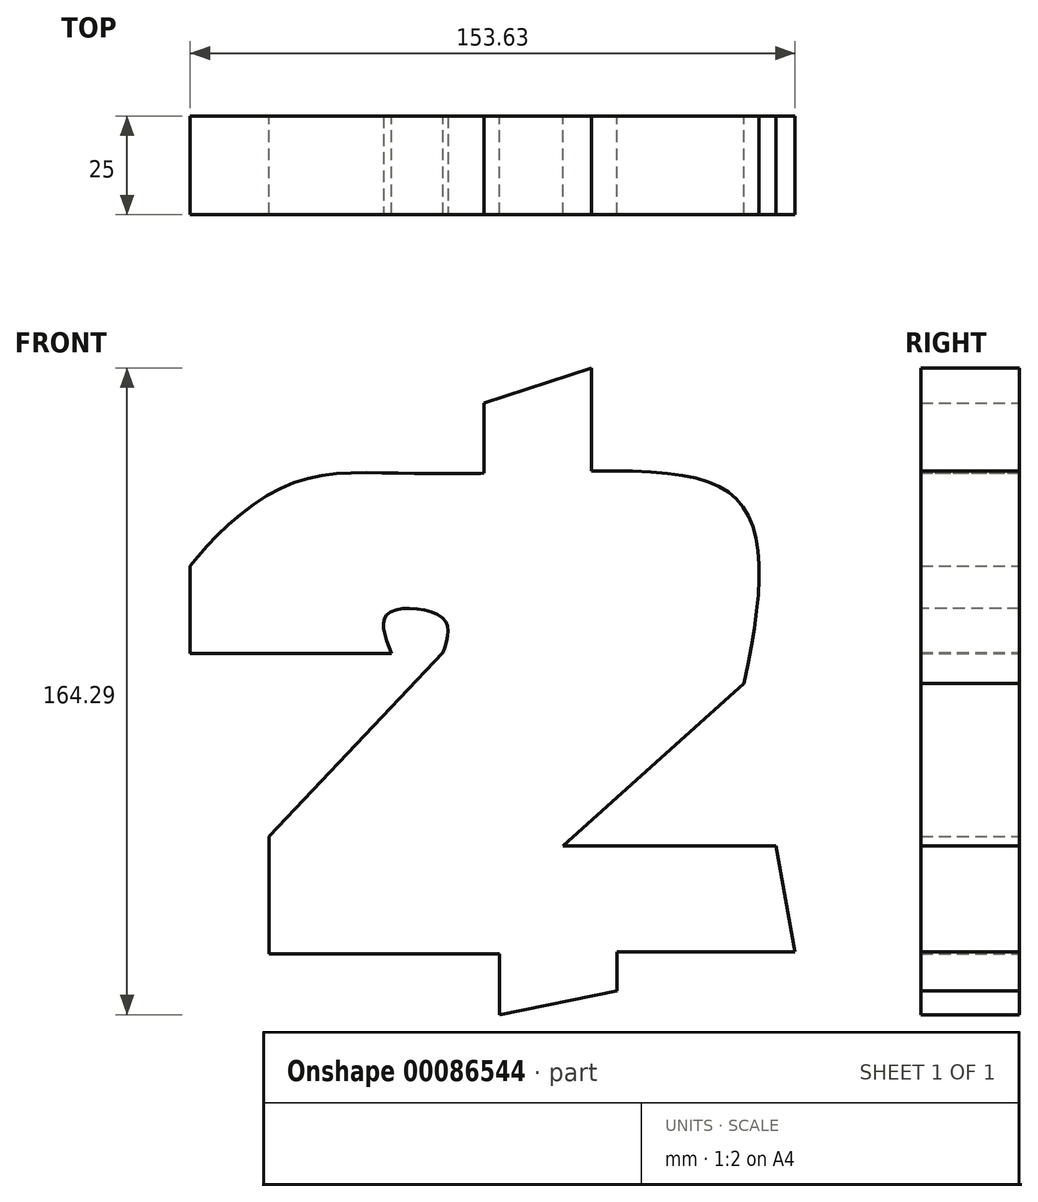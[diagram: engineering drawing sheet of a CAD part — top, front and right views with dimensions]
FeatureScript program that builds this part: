
annotation { "Feature Type Name" : "Feature", "Feature Type Description" : "" }
export const myFeature = defineFeature(function(context is Context, id is Id, definition is map)
    precondition{}
    {
        {
            var Q0;
            Q0=qCreatedBy(makeId("Front.planeOp"),FACE);
            var sketch = newSketch(context, id + "F0", { "sketchPlane" : qUnion([Q0])});
            skLineSegment(sketch, "E0", {"start": v(-74.64, -29.84) * mm, "end": v(-16.06, -29.84) * mm});
            skLineSegment(sketch, "E1", {"start": v(13.73, -29.27) * mm, "end": v(58.97, -29.27) * mm});
            skLineSegment(sketch, "E2", {"start": v(58.97, -29.27) * mm, "end": v(54.19, -2.4) * mm});
            skLineSegment(sketch, "E3", {"start": v(54.19, -2.4) * mm, "end": v(0, -2.4) * mm});
            skLineSegment(sketch, "E4", {"start": v(-74.64, -29.84) * mm, "end": v(-74.64, 0) * mm});
            skLineSegment(sketch, "E5", {"start": v(-16.06, -29.84) * mm, "end": v(-16.06, -45.27) * mm});
            skLineSegment(sketch, "E6", {"start": v(-16.06, -45.27) * mm, "end": v(13.73, -39.19) * mm});
            skLineSegment(sketch, "E7", {"start": v(13.73, -39.19) * mm, "end": v(13.73, -29.27) * mm});
            skLineSegment(sketch, "E8", {"start": v(-74.64, 0) * mm, "end": v(-30.42, 46.72) * mm});
            skLineSegment(sketch, "E9", {"start": v(0, -2.4) * mm, "end": v(46.09, 38.92) * mm});
            skLineSegment(sketch, "E10", {"start": v(-43.51, 46.53) * mm, "end": v(-94.66, 46.53) * mm});
            skFitSpline(sketch, "E11", {"points": [v(-30.42, 46.72) * mm, v(-30.42, 55.4) * mm, v(-44.36, 56.67) * mm, v(-43.51, 46.53) * mm], "startDerivative": vector(11.3, 33.02) * mm, "endDerivative": vector(15, -38.27) * mm});
            skLineSegment(sketch, "E12", {"start": v(-94.66, 46.53) * mm, "end": v(-94.66, 68.75) * mm});
            skFitSpline(sketch, "E13", {"points": [v(-94.66, 68.75) * mm, v(-71.1, 88.76) * mm, v(-40.39, 92.28) * mm, v(-20.01, 92.29) * mm], "startDerivative": vector(40.17, 52.53) * mm, "endDerivative": vector(6.6, 0.16) * mm});
            skLineSegment(sketch, "E14", {"start": v(-20.01, 92.29) * mm, "end": v(-20.01, 110.1) * mm});
            skLineSegment(sketch, "E15", {"start": v(-20.01, 110.1) * mm, "end": v(7.3, 119.02) * mm});
            skLineSegment(sketch, "E16", {"start": v(7.3, 119.02) * mm, "end": v(7.3, 92.85) * mm});
            skFitSpline(sketch, "E17", {"points": [v(46.09, 38.92) * mm, v(46.09, 83.34) * mm, v(7.3, 92.85) * mm], "startDerivative": vector(24.31, 111.72) * mm, "endDerivative": vector(-129.71, -1.86) * mm});
            skSolve(sketch);
        }
        {
            var Q0;
            Q0 = qSketchRegion(id + "F0", true);
            extrude(context, id + "F1", {"entities" : qUnion([Q0]), "depth" : 25 * mm});
        }
    });
